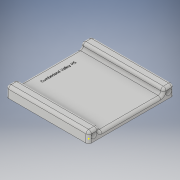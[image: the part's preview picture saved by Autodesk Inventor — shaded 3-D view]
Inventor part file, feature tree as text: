
AUTODESK INVENTOR PART (.ipt)
format: ipt  version: 2018 (Build 220112000, 112)  size: 191,488 bytes
history: native  units: in
note: dims shown in document units (in); Inventor stores cm internally (conversion verified against a paired STEP export)
features: fillet x8, sketch x4, extrude x2, hole x1
ambient origin geometry x8: Origin, YZ Plane, XZ Plane, XY Plane, X Axis, Y Axis, Z Axis, Center Point
bodies: Solid1 (feature_tree)
feature tree (15):
  extrude  "Extrusion1"  Depth=4.0in
  extrude  "Extrusion2"  Depth=0.5in
  hole  "Hole1"  [1 undecoded]
  fillet  "Fillet1"  Radius=0.125in
  fillet  "Fillet2"  Radius=0.125in
  fillet  "Fillet3"  Radius=0.125in
  fillet  "Fillet4"  Radius=0.125in
  fillet  "Fillet5"  Radius=0.125in
  fillet  "Fillet6"  Radius=0.125in
  fillet  "Fillet7"  Radius=0.125in
  fillet  "Fillet8"  Radius=0.125in
  sketch  "Sketch4"  dims[d8=0.26in d9=0.75in d10=0.375in d11=0.25in d12=0.5635in d13=1.0in d14=0.8108in d15=0.125in d16=0.125in d17=0.125in d18=0.125in d19=0.125in d20=0.125in d21=0.125in d22=0.125in]
  sketch  "Sketch1"  dims[d0=3.875in d1=4.0in]
  sketch  "Sketch2"  dims[d2=0.25in d3=0.0in d4=0.5in]
  sketch  "Sketch3"  dims[d5=0.5in d6=0.25in d7=0.0in]
note: 1 required parameter value undecoded (feature->parameter linkage not recoverable at this tier; creation-order binding heuristic only, values carry confidence <= 0.55)
